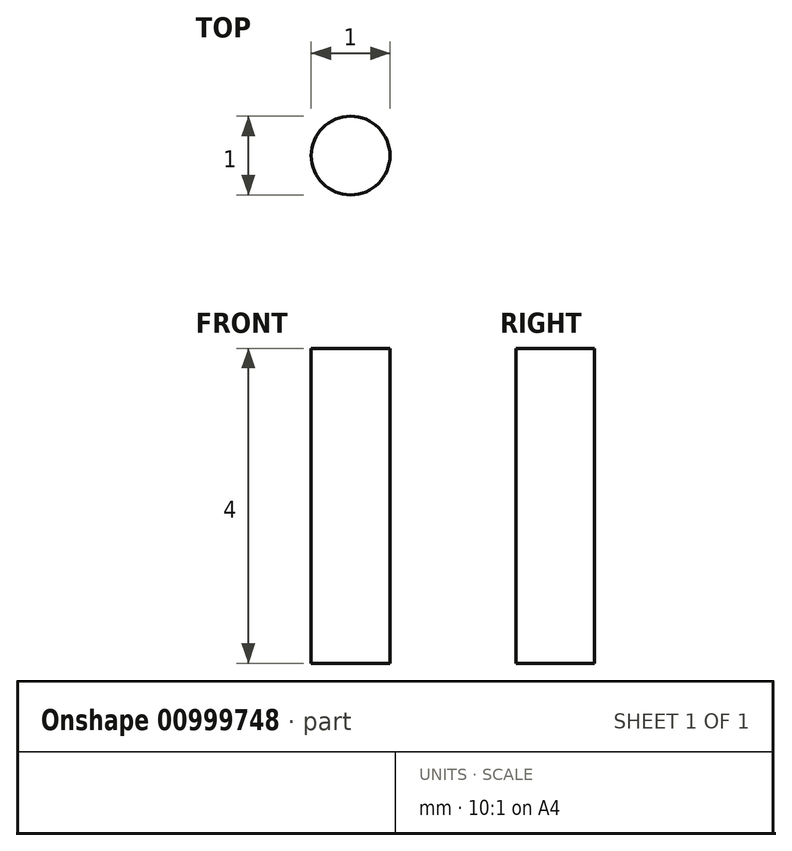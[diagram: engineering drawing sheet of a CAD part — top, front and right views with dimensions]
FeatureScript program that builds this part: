
annotation { "Feature Type Name" : "Feature", "Feature Type Description" : "" }
export const myFeature = defineFeature(function(context is Context, id is Id, definition is map)
    precondition{}
    {
        {
            var Q0;
            Q0=qCreatedBy(makeId("Top.planeOp"),FACE);
            var sketch = newSketch(context, id + "F0", { "sketchPlane" : qUnion([Q0])});
            skCircle(sketch, "E0", {"center": v(0, 0) * mm, "radius": 0.5 * mm});
            skSolve(sketch);
        }
        {
            var Q0;
            Q0 = qSketchRegion(id + "F0", true);
            extrude(context, id + "F1", {"entities" : qUnion([Q0]), "depth" : 4 * mm, "offsetDistance" : 25 * mm});
        }
    });
